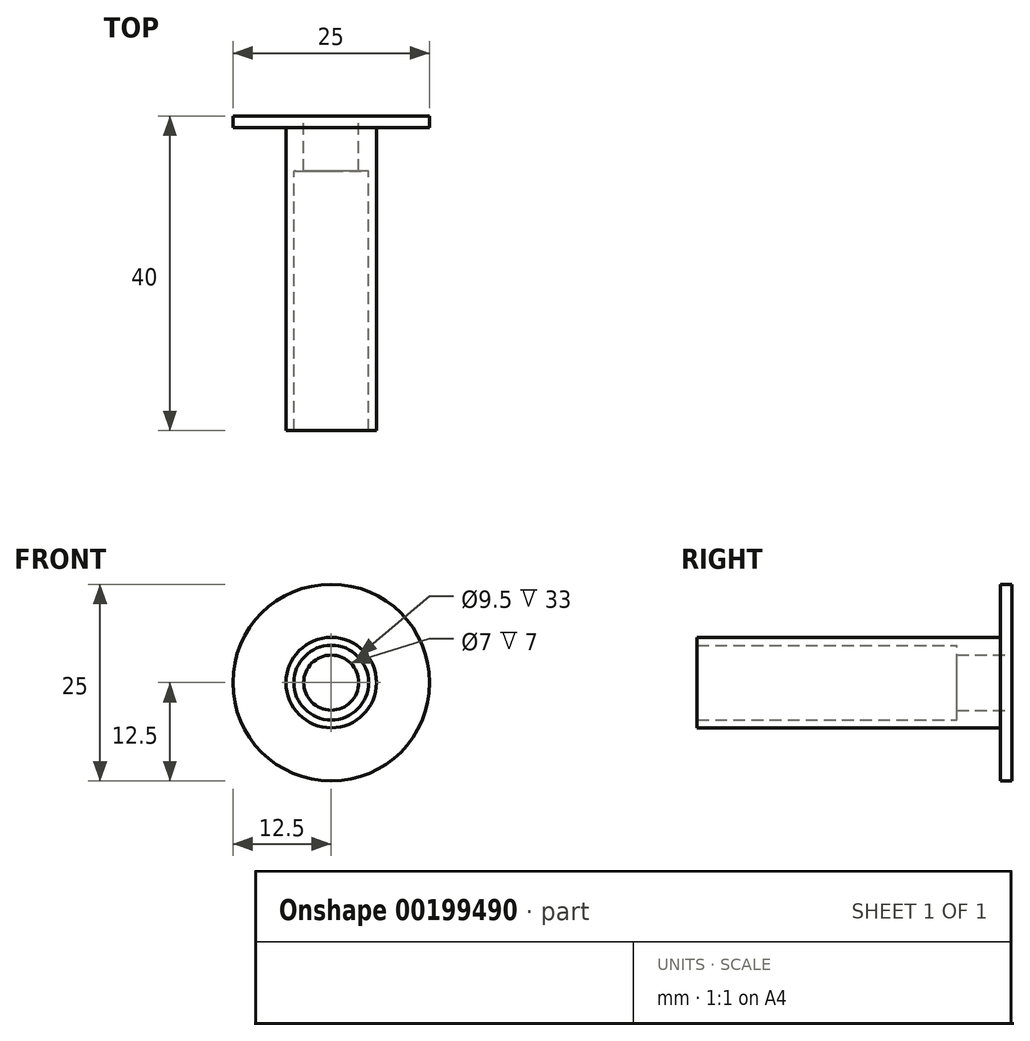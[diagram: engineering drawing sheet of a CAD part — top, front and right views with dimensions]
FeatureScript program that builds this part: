
annotation { "Feature Type Name" : "Feature", "Feature Type Description" : "" }
export const myFeature = defineFeature(function(context is Context, id is Id, definition is map)
    precondition{}
    {
        {
            var Q0;
            Q0=qCreatedBy(makeId("Front.planeOp"),FACE);
            var sketch = newSketch(context, id + "F0", { "sketchPlane" : qUnion([Q0])});
            skCircle(sketch, "E0", {"center": v(0, 0) * mm, "radius": 12.5 * mm});
            skCircle(sketch, "E1", {"center": v(0, 0) * mm, "radius": 5.75 * mm});
            skCircle(sketch, "E2", {"center": v(0, 0) * mm, "radius": 4.75 * mm});
            skCircle(sketch, "E3", {"center": v(0, 0) * mm, "radius": 3.5 * mm});
            skSolve(sketch);
        }
        {
            var Q0;
            Q0=makeQuery(id+"F0.imprint","IMPRINT",FACE,{"disambiguationData":[TD([[makeQuery(id+"F0.imprint","IMPRINT",EDGE,{"derivedFrom":sQuery(id+"F0.wireOp",EDGE,"E1")}),1.0]])]});
            var Q1;
            Q1=makeQuery(id+"F0.imprint","IMPRINT",FACE,{"disambiguationData":[TD([[makeQuery(id+"F0.imprint","IMPRINT",EDGE,{"derivedFrom":sQuery(id+"F0.wireOp",EDGE,"E0")}),1.0]])]});
            extrude(context, id + "F1", {"entities" : qUnion([Q0, Q1]), "depth" : 1.5 * mm});
        }
        {
            var Q0;
            Q0=makeQuery(id+"F0.imprint","IMPRINT",FACE,{"disambiguationData":[TD([[makeQuery(id+"F0.imprint","IMPRINT",EDGE,{"derivedFrom":sQuery(id+"F0.wireOp",EDGE,"E1")}),1.0]])]});
            extrude(context, id + "F2", {"entities" : qUnion([Q0]), "operationType" : NewBodyOperationType.ADD, "depth" : 40 * mm});
        }
        {
            var Q0;
            Q0=makeQuery(id+"F0.imprint","IMPRINT",FACE,{"disambiguationData":[TD([[makeQuery(id+"F0.imprint","IMPRINT",EDGE,{"derivedFrom":sQuery(id+"F0.wireOp",EDGE,"E2")}),1.0]])]});
            extrude(context, id + "F3", {"entities" : qUnion([Q0]), "operationType" : NewBodyOperationType.ADD, "depth" : 7 * mm});
        }
    });
